# Revit family: Screen-Teknion-CQCFS-Routes-Gathered_Fabric_Mobile_Screen-R2022
name_source: partatom
category: Furniture
units: mm (PartAtom-declared; Revit-internal decimal feet)

## family parameters
Always vertical = Yes
Cut with Voids When Loaded = No
OmniClass Number = 23.40.20.00
OmniClass Title = General Furniture and Specialties
Render Appearance Source = Family Geometry
Room Calculation Point = No
Shared = Yes
Work Plane-Based = No

## types (1)
- Gathered Fabric Mobile Screen
    Assembly Code = E2020200
    Default Elevation = 0 "
    Depth = 0 "
    Description = Gathered Mobile Fabric Screen - Routes
    Height = 60 "
    Length = 0 "
    Manufacturer = Teknion
    Manufacturer Fax = 416.661.4586
    Model = CQCFS6048
    Part Number = CQCFS
    Product Documentation Link = https://assets.teknion.com
    Product Line = Routes
    Product Page URL = https://www.teknion.com
    Series = Screen
    Sustainability Data = https://www.teknion.com
    URL = www.teknion.com
    Unit Weight URL = http://www.teknion.com
    Warranty = http://www.teknion.com
    Width = 0 "

## geometry (parser evidence)
native form markers: Sweep x3
no freeform markers — native parametric forms only
